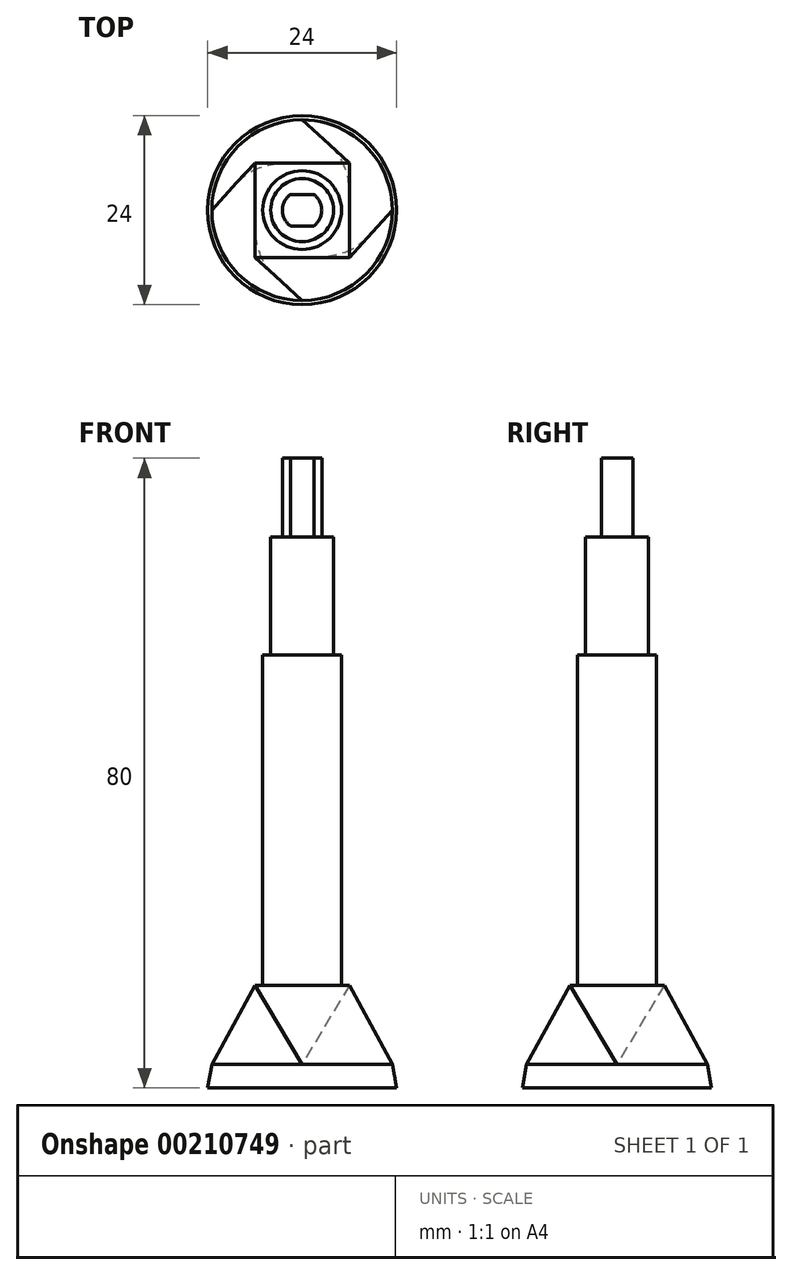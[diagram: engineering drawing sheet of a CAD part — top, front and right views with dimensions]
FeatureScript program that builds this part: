
annotation { "Feature Type Name" : "Feature", "Feature Type Description" : "" }
export const myFeature = defineFeature(function(context is Context, id is Id, definition is map)
    precondition{}
    {
        {
            var Q0;
            Q0=qCreatedBy(makeId("Top.planeOp"),FACE);
            var sketch = newSketch(context, id + "F0", { "sketchPlane" : qUnion([Q0])});
            skCircle(sketch, "E0", {"center": v(0, 0) * mm, "radius": 5 * mm});
            skSolve(sketch);
        }
        {
            var Q0;
            Q0 = qSketchRegion(id + "F0", true);
            extrude(context, id + "F1", {"entities" : qUnion([Q0]), "depth" : 80 * mm});
        }
        {
            var Q0;
            Q0=makeQuery(id+"F1.opExtrude","CAP_FACE",FACE,{"disambiguationData":[OSD([sQuery(id+"F0.wireOp",EDGE,"E0")])],"isStart":false});
            var sketch = newSketch(context, id + "F2", { "sketchPlane" : qUnion([Q0])});
            skCircle(sketch, "E1", {"center": v(0, 0) * mm, "radius": 4 * mm});
            skCircle(sketch, "E2", {"center": v(0, 0) * mm, "radius": 5 * mm});
            skSolve(sketch);
        }
        {
            var Q0;
            Q0=makeQuery(id+"F2.imprint","IMPRINT",FACE,{"disambiguationData":[TD([[makeQuery(id+"F2.imprint","IMPRINT",EDGE,{"derivedFrom":sQuery(id+"F2.wireOp",EDGE,"E1")}),-1.0]])]});
            extrude(context, id + "F3", {"entities" : qUnion([Q0]), "operationType" : NewBodyOperationType.REMOVE, "oppositeDirection" : true, "depth" : 25 * mm});
        }
        {
            var Q0;
            Q0=makeQuery(id+"F1.opExtrude","CAP_FACE",FACE,{"disambiguationData":[OSD([sQuery(id+"F0.wireOp",EDGE,"E0")])],"isStart":false});
            var sketch = newSketch(context, id + "F4", { "sketchPlane" : qUnion([Q0])});
            skCircle(sketch, "E3", {"center": v(0, 0) * mm, "radius": 5 * mm});
            skCircle(sketch, "E4", {"center": v(0, 0) * mm, "radius": 2.5 * mm});
            skLineSegment(sketch, "E5", {"start": v(-1.5, 2) * mm, "end": v(1.5, 2) * mm});
            skLineSegment(sketch, "E6", {"start": v(-1.5, -2) * mm, "end": v(1.5, -2) * mm});
            skSolve(sketch);
        }
        {
            var Q0;
            Q0 = qSketchRegion(id + "F4", true);
            var Q1;
            {var subQ0=sQuery(id+"F4.wireOp",EDGE,"E5");Q1=makeQuery(id+"F4.imprint","IMPRINT",FACE,{"disambiguationData":[TD([[makeQuery(id+"F4.imprint","IMPRINT",EDGE,{"derivedFrom":subQ0}),1.0]])]});}
            var Q2;
            {var subQ0=sQuery(id+"F4.wireOp",EDGE,"E6");Q2=makeQuery(id+"F4.imprint","IMPRINT",FACE,{"disambiguationData":[TD([[makeQuery(id+"F4.imprint","IMPRINT",EDGE,{"derivedFrom":subQ0}),-1.0]])]});}
            extrude(context, id + "F5", {"entities" : qUnion([Q0, Q1, Q2]), "operationType" : NewBodyOperationType.REMOVE, "oppositeDirection" : true, "depth" : 10 * mm});
        }
        {
            var Q0;
            Q0=qCreatedBy(makeId("Top.planeOp"),FACE);
            var sketch = newSketch(context, id + "F6", { "sketchPlane" : qUnion([Q0])});
            skCircle(sketch, "E7", {"center": v(0, 0) * mm, "radius": 12 * mm});
            skSolve(sketch);
        }
        {
            var Q0;
            Q0 = qSketchRegion(id + "F6", true);
            extrude(context, id + "F7", {"entities" : qUnion([Q0]), "operationType" : NewBodyOperationType.ADD, "depth" : 3 * mm, "hasDraft" : true, "draftAngle" : 10 * degree, "draftPullDirection" : true});
        }
        {
            var Q0;
            Q0=qCreatedBy(makeId("Top.planeOp"),FACE);
            cPlane(context, id + "F8", {"entities" : qUnion([Q0]), "cplaneType" : CPlaneType.OFFSET, "offset" : 13 * mm, "width" : 150 * mm, "height" : 150 * mm});
        }
        {
            var Q0;
            Q0=qCreatedBy(id+"F8.planeOp",FACE);
            var sketch = newSketch(context, id + "F9", { "sketchPlane" : qUnion([Q0])});
            skLineSegment(sketch, "E8.bottom", {"start": v(6, -6) * mm, "end": v(-6, -6) * mm});
            skLineSegment(sketch, "E8.top", {"start": v(6, 6) * mm, "end": v(-6, 6) * mm});
            skLineSegment(sketch, "E8.left", {"start": v(6, -6) * mm, "end": v(6, 6) * mm});
            skLineSegment(sketch, "E8.right", {"start": v(-6, -6) * mm, "end": v(-6, 6) * mm});
            skPoint(sketch, "E8.middle", {"position": v(0, 0) * mm});
            skSolve(sketch);
        }
        {
            var Q0;
            Q0=makeQuery(id+"F7.opExtrude","CAP_FACE",FACE,{"disambiguationData":[OSD([sQuery(id+"F6.wireOp",EDGE,"E7")])],"isStart":false});
            var sketch = newSketch(context, id + "F10", { "sketchPlane" : qUnion([Q0])});
            skCircle(sketch, "E9", {"center": v(0, 0) * mm, "radius": 11.47 * mm});
            skCircle(sketch, "E10.cCircle", {"center": v(0, 0) * mm, "radius": 11.47 * mm, "construction": true});
            skLineSegment(sketch, "E10.0", {"start": v(11.47, 0) * mm, "end": v(0, -11.47) * mm});
            skLineSegment(sketch, "E10.1", {"start": v(0, -11.47) * mm, "end": v(-11.47, 0) * mm});
            skLineSegment(sketch, "E10.2", {"start": v(-11.47, 0) * mm, "end": v(0, 11.47) * mm});
            skLineSegment(sketch, "E10.3", {"start": v(0, 11.47) * mm, "end": v(11.47, 0) * mm});
            skSolve(sketch);
        }
        {
            var Q0;
            Q0=makeQuery(id+"F10.imprint","IMPRINT",FACE,{"disambiguationData":[TD([[makeQuery(id+"F10.imprint","IMPRINT",EDGE,{"derivedFrom":sQuery(id+"F10.wireOp",EDGE,"E10.0")}),-1.0]])]});
            var sketch = newSketch(context, id + "F11", { "sketchPlane" : qUnion([Q0])});
            skCircle(sketch, "E11", {"center": v(0, 0) * mm, "radius": 11.47 * mm});
            skSolve(sketch);
        }
        {
            var Q1;
            Q1 = qSketchRegion(id + "F9", true);
            var Q2;
            Q2 = qSketchRegion(id + "F11", true);
            var Q3;
            Q3=sQuery(id+"F9.wireOp",VERTEX,"E8.right.start");
            var Q4;
            Q4=sQuery(id+"F10.wireOp",VERTEX,"E10.1.start");
            loft(context, id + "F12", {"operationType" : NewBodyOperationType.ADD, "sheetProfilesArray" : [{ "sheetProfileEntities" : qUnion([Q1]) }, { "sheetProfileEntities" : qUnion([Q2]) }], "matchConnections" : true, "connections" : [{ "connectionEntities" : qUnion([Q3, Q4]), "connectionEdgeQueries" : qUnion([]), "connectionEdgeParameters" : [] }]});
        }
    });
